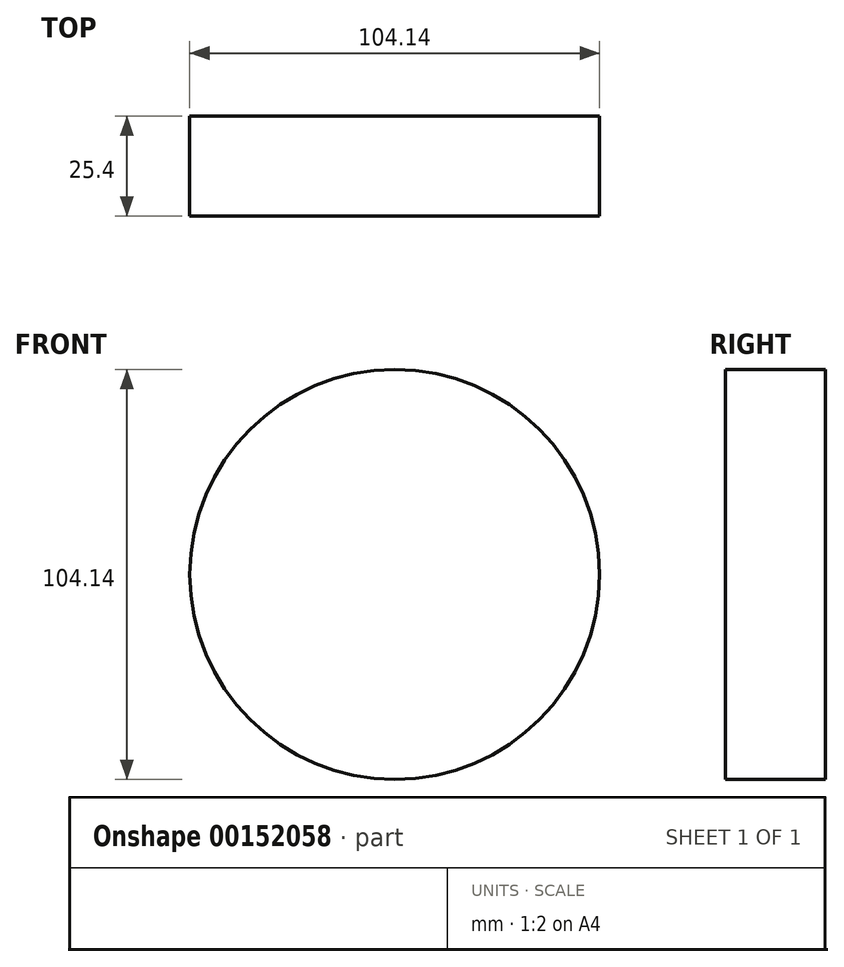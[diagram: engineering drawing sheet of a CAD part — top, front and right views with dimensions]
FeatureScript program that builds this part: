
annotation { "Feature Type Name" : "Feature", "Feature Type Description" : "" }
export const myFeature = defineFeature(function(context is Context, id is Id, definition is map)
    precondition{}
    {
        {
            var Q0;
            Q0=qCreatedBy(makeId("Front.planeOp"),FACE);
            var sketch = newSketch(context, id + "F0", { "sketchPlane" : qUnion([Q0])});
            skCircle(sketch, "E0", {"center": v(0, 0) * mm, "radius": 52.07 * mm});
            skSolve(sketch);
        }
        {
            var Q0;
            Q0 = qSketchRegion(id + "F0", true);
            extrude(context, id + "F1", {"entities" : qUnion([Q0]), "depth" : 25.4 * mm});
        }
    });
